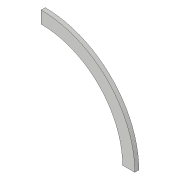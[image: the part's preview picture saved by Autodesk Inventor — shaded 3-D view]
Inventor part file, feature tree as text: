
AUTODESK INVENTOR PART (.ipt)
format: ipt  version: 2018 (Build 220112000, 112)  size: 101,888 bytes
history: native  units: in
note: dims shown in document units (in); Inventor stores cm internally (conversion verified against a paired STEP export)
features: extrude x1, sketch x1
ambient origin geometry x8: Origin, YZ Plane, XZ Plane, XY Plane, X Axis, Y Axis, Z Axis, Center Point
bodies: Solid1 (feature_tree)
feature tree (2):
  extrude  "Extrusion1"  Depth=0.1969in
  sketch  "Sketch1"  dims[d0=7.874in d1=9.0551in d2=0.1969in d3=0.0in]
